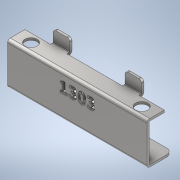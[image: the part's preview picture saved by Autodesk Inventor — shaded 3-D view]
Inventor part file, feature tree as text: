
AUTODESK INVENTOR PART (.ipt)
format: ipt  version: 2020 (Build 240168000, 168)  size: 567,296 bytes
history: native  units: mm
features: other x5, extrude x3, fillet x1, sketch x1, projected_geometry x1
ambient origin geometry x8: Origin, YZ Plane, XZ Plane, XY Plane, X Axis, Y Axis, Z Axis, Center Point
bodies: Body1 (feature_tree)
feature tree (11):
  other  "實體1"
  extrude  "擠出1"  Depth=126.0mm
  extrude  "擠出3"  Depth=21.3mm
  extrude  "擠出4"  Depth=33.0mm
  other  "折彎零件3"
  other  "折彎零件1"
  other  "折彎零件2"
  fillet  "圓角1"  Radius=14.0mm
  sketch  "草圖4"
  projected_geometry  "投影迴路1"
  other  "定義1"
